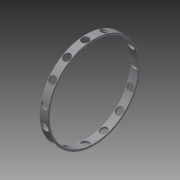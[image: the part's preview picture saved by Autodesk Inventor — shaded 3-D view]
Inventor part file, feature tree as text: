
AUTODESK INVENTOR PART (.ipt)
format: ipt  version: 2014 SP2 (Build 180246200, 246)  size: 261,632 bytes
history: native  units: mm
features: other x112, revolve x2, sketch x2, pattern_circular x1
ambient origin geometry x8: Origin, YZ Plane, XZ Plane, XY Plane, X Axis, Y Axis, Z Axis, Center Point
bodies: Solid1 (feature_tree)
feature tree (117):
  revolve  "Revolution1"  Angle=360.0deg
  revolve  "Revolution2"  [1 undecoded]
  pattern_circular  "Circular Pattern1"  [2 undecoded]
  other  "1_XY"
  other  "1_YZ"
  other  "1_ZX"
  other  "1_X"
  other  "1_Y"
  other  "1_Z"
  other  "1_Center"
  other  "2_1_XY"
  other  "2_1_YZ"
  other  "2_1_ZX"
  other  "2_1_X"
  other  "2_1_Y"
  other  "2_1_Z"
  other  "2_1_Center"
  other  "2_10_XY"
  other  "2_10_YZ"
  other  "2_10_ZX"
  other  "2_10_X"
  other  "2_10_Y"
  other  "2_10_Z"
  other  "2_10_Center"
  other  "2_11_XY"
  other  "2_11_YZ"
  other  "2_11_ZX"
  other  "2_11_X"
  other  "2_11_Y"
  other  "2_11_Z"
  other  "2_11_Center"
  other  "2_12_XY"
  other  "2_12_YZ"
  other  "2_12_ZX"
  other  "2_12_X"
  other  "2_12_Y"
  other  "2_12_Z"
  other  "2_12_Center"
  other  "2_13_XY"
  other  "2_13_YZ"
  other  "2_13_ZX"
  other  "2_13_X"
  other  "2_13_Y"
  other  "2_13_Z"
  other  "2_13_Center"
  other  "2_14_XY"
  other  "2_14_YZ"
  other  "2_14_ZX"
  other  "2_14_X"
  other  "2_14_Y"
  other  "2_14_Z"
  other  "2_14_Center"
  other  "2_15_XY"
  other  "2_15_YZ"
  other  "2_15_ZX"
  other  "2_15_X"
  other  "2_15_Y"
  other  "2_15_Z"
  other  "2_15_Center"
  other  "2_2_XY"
  other  "2_2_YZ"
  other  "2_2_ZX"
  other  "2_2_X"
  other  "2_2_Y"
  other  "2_2_Z"
  other  "2_2_Center"
  other  "2_3_XY"
  other  "2_3_YZ"
  other  "2_3_ZX"
  other  "2_3_X"
  other  "2_3_Y"
  other  "2_3_Z"
  other  "2_3_Center"
  other  "2_4_XY"
  other  "2_4_YZ"
  other  "2_4_ZX"
  other  "2_4_X"
  other  "2_4_Y"
  other  "2_4_Z"
  other  "2_4_Center"
  other  "2_5_XY"
  other  "2_5_YZ"
  other  "2_5_ZX"
  other  "2_5_X"
  other  "2_5_Y"
  other  "2_5_Z"
  other  "2_5_Center"
  other  "2_6_XY"
  other  "2_6_YZ"
  other  "2_6_ZX"
  other  "2_6_X"
  other  "2_6_Y"
  other  "2_6_Z"
  other  "2_6_Center"
  other  "2_7_XY"
  other  "2_7_YZ"
  other  "2_7_ZX"
  other  "2_7_X"
  other  "2_7_Y"
  other  "2_7_Z"
  other  "2_7_Center"
  other  "2_8_XY"
  other  "2_8_YZ"
  other  "2_8_ZX"
  other  "2_8_X"
  other  "2_8_Y"
  other  "2_8_Z"
  other  "2_8_Center"
  other  "2_9_XY"
  other  "2_9_YZ"
  other  "2_9_ZX"
  other  "2_9_X"
  other  "2_9_Y"
  other  "2_9_Z"
  other  "2_9_Center"
  sketch  "Sketch_6"  dims[d2=150.0mm d3=4.18879mm]
  sketch  "Sketch_2"  dims[d0=360.0deg d1=360.0deg]
note: 3 required parameter values undecoded (feature->parameter linkage not recoverable at this tier; creation-order binding heuristic only, values carry confidence <= 0.55)
